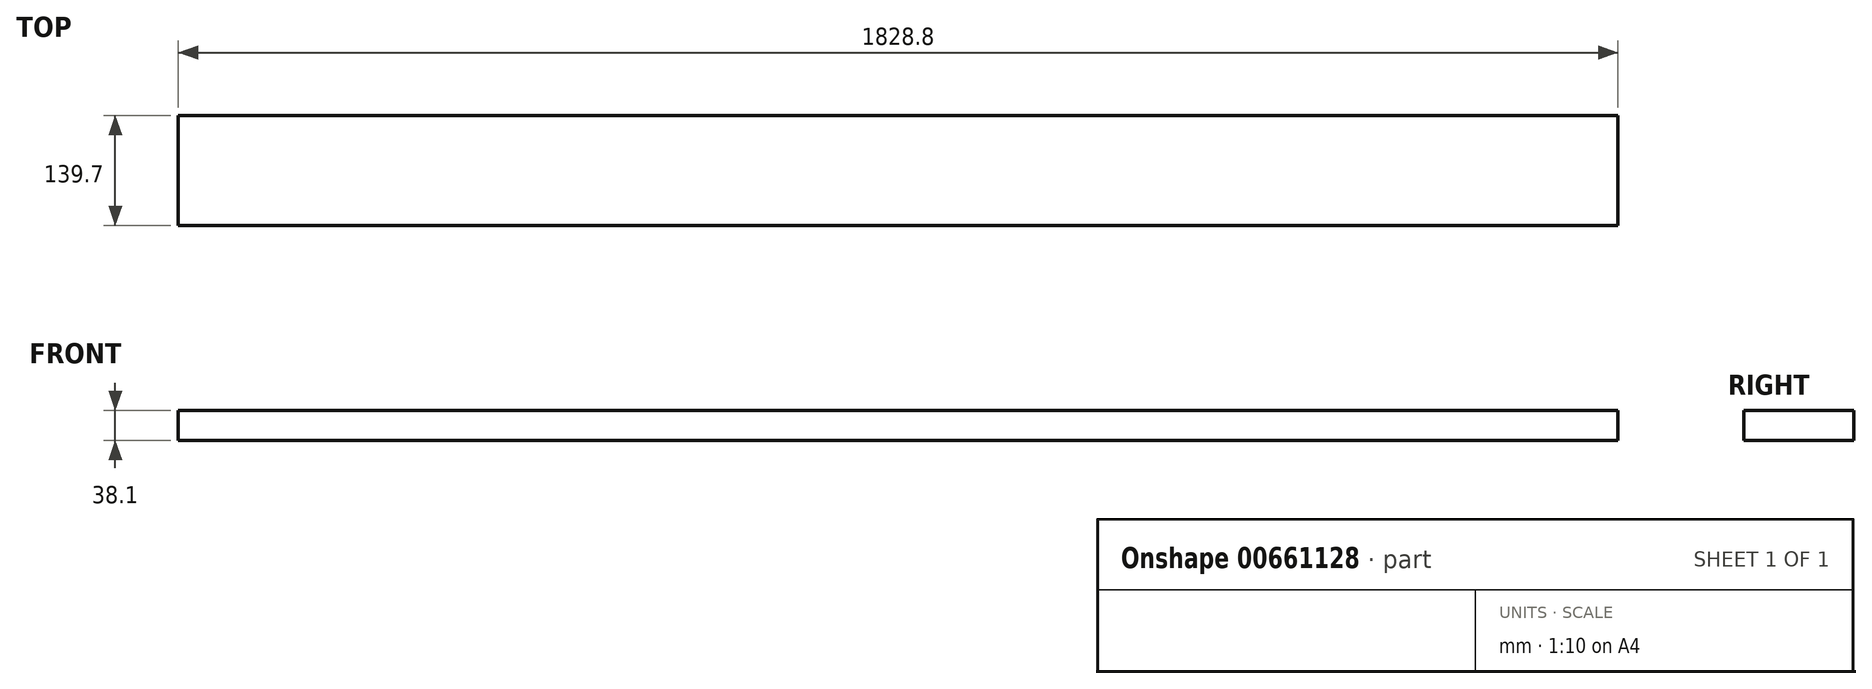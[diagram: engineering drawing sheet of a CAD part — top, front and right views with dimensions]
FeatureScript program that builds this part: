
annotation { "Feature Type Name" : "Feature", "Feature Type Description" : "" }
export const myFeature = defineFeature(function(context is Context, id is Id, definition is map)
    precondition{}
    {
        {
            var Q0;
            Q0=qCreatedBy(makeId("Front.planeOp"),FACE);
            var sketch = newSketch(context, id + "F0", { "sketchPlane" : qUnion([Q0])});
            skLineSegment(sketch, "E0.bottom", {"start": v(-914.4, 19.05) * mm, "end": v(914.4, 19.05) * mm});
            skLineSegment(sketch, "E0.top", {"start": v(-914.4, -19.05) * mm, "end": v(914.4, -19.05) * mm});
            skLineSegment(sketch, "E0.left", {"start": v(-914.4, 19.05) * mm, "end": v(-914.4, -19.05) * mm});
            skLineSegment(sketch, "E0.right", {"start": v(914.4, 19.05) * mm, "end": v(914.4, -19.05) * mm});
            skPoint(sketch, "E0.middle", {"position": v(0, 0) * mm});
            skSolve(sketch);
        }
        {
            var Q0;
            Q0 = qSketchRegion(id + "F0", true);
            extrude(context, id + "F1", {"entities" : qUnion([Q0]), "endBound" : BoundingType.SYMMETRIC, "depth" : 139.7 * mm, "offsetDistance" : 25.4 * mm});
        }
    });
